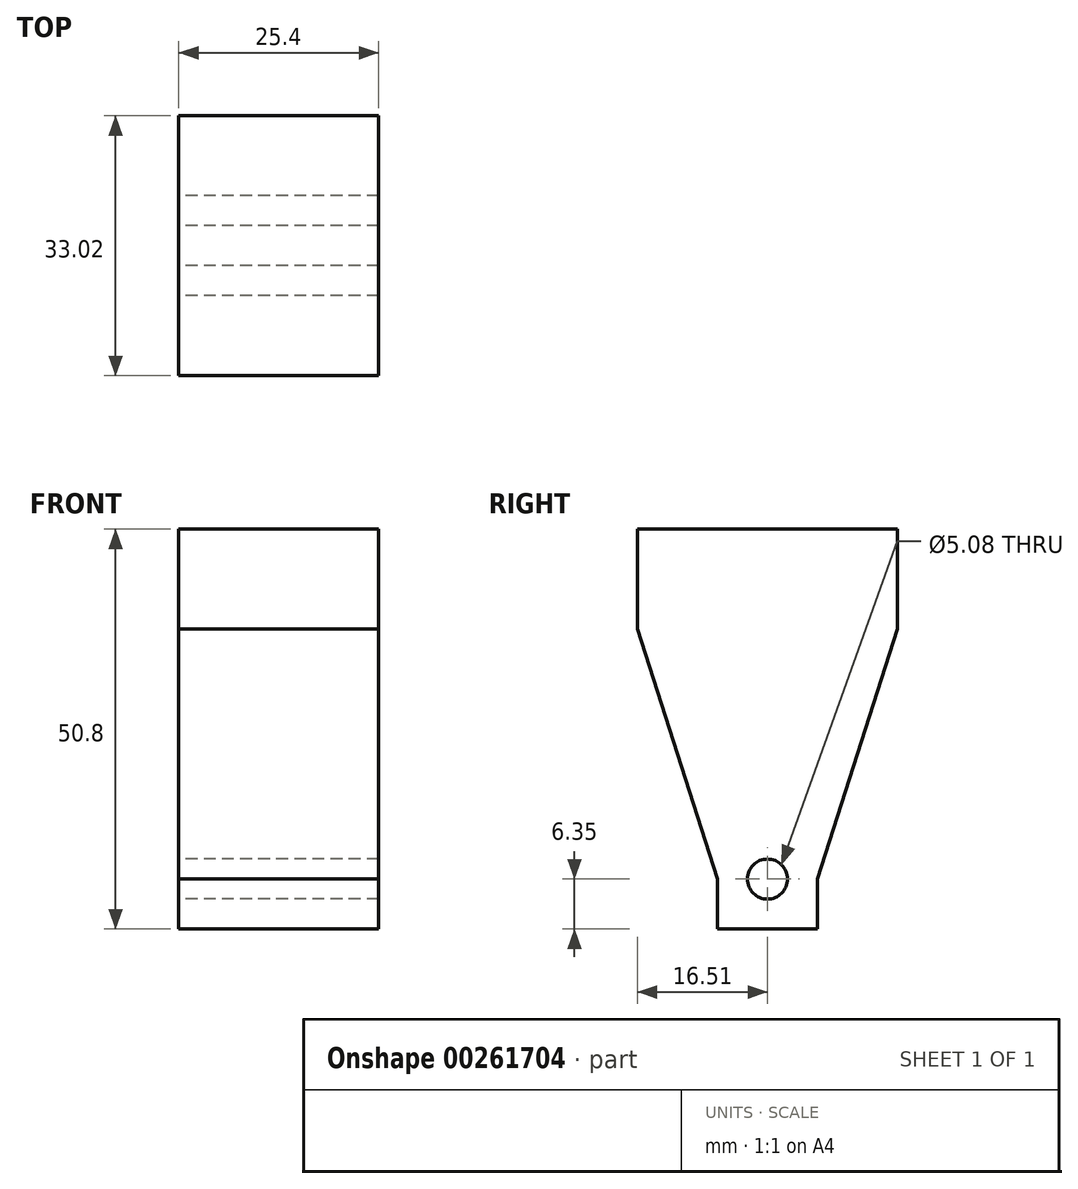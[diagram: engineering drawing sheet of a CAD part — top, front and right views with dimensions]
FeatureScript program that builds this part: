
annotation { "Feature Type Name" : "Feature", "Feature Type Description" : "" }
export const myFeature = defineFeature(function(context is Context, id is Id, definition is map)
    precondition{}
    {
        {
            var Q0;
            Q0=qCreatedBy(makeId("Right.planeOp"),FACE);
            var sketch = newSketch(context, id + "F0", { "sketchPlane" : qUnion([Q0])});
            skLineSegment(sketch, "E0.bottom", {"start": v(0, 0) * mm, "end": v(12.7, 0) * mm});
            skLineSegment(sketch, "E0.top", {"start": v(0, -50.8) * mm, "end": v(12.7, -50.8) * mm});
            skLineSegment(sketch, "E0.left", {"start": v(0, 0) * mm, "end": v(0, -50.8) * mm});
            skLineSegment(sketch, "E0.right", {"start": v(12.7, 0) * mm, "end": v(12.7, -50.8) * mm});
            skLineSegment(sketch, "E1", {"start": v(6.35, 0) * mm, "end": v(6.35, -50.8) * mm});
            skLineSegment(sketch, "E2", {"start": v(0, -44.45) * mm, "end": v(12.7, -44.45) * mm});
            skCircle(sketch, "E3", {"center": v(6.35, -44.45) * mm, "radius": 2.54 * mm});
            skLineSegment(sketch, "E4.bottom", {"start": v(0, 0) * mm, "end": v(22.86, 0) * mm});
            skLineSegment(sketch, "E4.top", {"start": v(0, -12.7) * mm, "end": v(22.86, -12.7) * mm});
            skLineSegment(sketch, "E4.left", {"start": v(0, 0) * mm, "end": v(0, -12.7) * mm});
            skLineSegment(sketch, "E4.right", {"start": v(22.86, 0) * mm, "end": v(22.86, -12.7) * mm});
            skLineSegment(sketch, "E5.bottom", {"start": v(12.7, 0) * mm, "end": v(-10.16, 0) * mm});
            skLineSegment(sketch, "E5.top", {"start": v(12.7, -12.7) * mm, "end": v(-10.16, -12.7) * mm});
            skLineSegment(sketch, "E5.left", {"start": v(12.7, 0) * mm, "end": v(12.7, -12.7) * mm});
            skLineSegment(sketch, "E5.right", {"start": v(-10.16, 0) * mm, "end": v(-10.16, -12.7) * mm});
            skLineSegment(sketch, "E6", {"start": v(-10.16, -12.7) * mm, "end": v(0, -44.45) * mm});
            skLineSegment(sketch, "E7", {"start": v(22.86, -12.7) * mm, "end": v(12.7, -44.45) * mm});
            skSolve(sketch);
        }
        {
            var Q0;
            Q0 = qSketchRegion(id + "F0", true);
            extrude(context, id + "F1", {"entities" : qUnion([Q0]), "depth" : 25.4 * mm});
        }
    });
